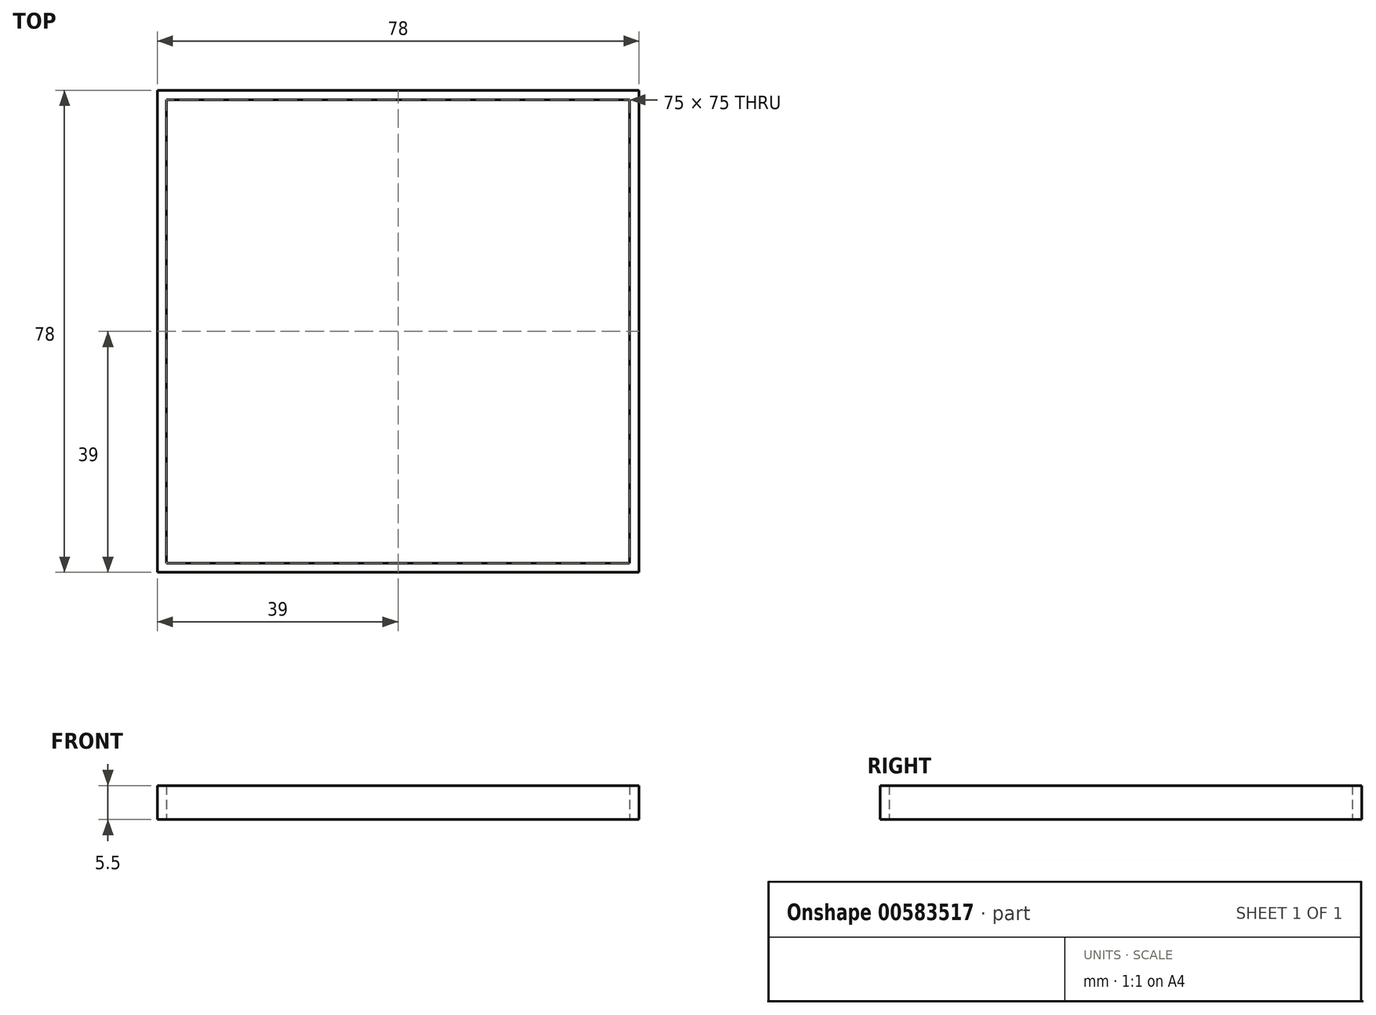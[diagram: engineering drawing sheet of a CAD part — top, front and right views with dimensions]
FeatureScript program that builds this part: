
annotation { "Feature Type Name" : "Feature", "Feature Type Description" : "" }
export const myFeature = defineFeature(function(context is Context, id is Id, definition is map)
    precondition{}
    {
        {
            var Q0;
            Q0=qCreatedBy(makeId("Top.planeOp"),FACE);
            var sketch = newSketch(context, id + "F0", { "sketchPlane" : qUnion([Q0])});
            skLineSegment(sketch, "E0.bottom", {"start": v(37.5, -37.5) * mm, "end": v(-37.5, -37.5) * mm});
            skLineSegment(sketch, "E0.top", {"start": v(37.5, 37.5) * mm, "end": v(-37.5, 37.5) * mm});
            skLineSegment(sketch, "E0.left", {"start": v(37.5, -37.5) * mm, "end": v(37.5, 37.5) * mm});
            skLineSegment(sketch, "E0.right", {"start": v(-37.5, -37.5) * mm, "end": v(-37.5, 37.5) * mm});
            skPoint(sketch, "E0.middle", {"position": v(0, 0) * mm});
            skLineSegment(sketch, "E1.bottom", {"start": v(39, -39) * mm, "end": v(-39, -39) * mm});
            skLineSegment(sketch, "E1.top", {"start": v(39, 39) * mm, "end": v(-39, 39) * mm});
            skLineSegment(sketch, "E1.left", {"start": v(39, -39) * mm, "end": v(39, 39) * mm});
            skLineSegment(sketch, "E1.right", {"start": v(-39, -39) * mm, "end": v(-39, 39) * mm});
            skSolve(sketch);
        }
        {
            var Q0;
            Q0 = qSketchRegion(id + "F0", true);
            extrude(context, id + "F1", {"entities" : qUnion([Q0]), "depth" : 5.5 * mm, "offsetDistance" : 25 * mm});
        }
    });
